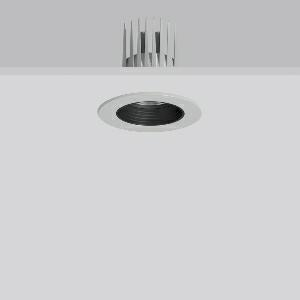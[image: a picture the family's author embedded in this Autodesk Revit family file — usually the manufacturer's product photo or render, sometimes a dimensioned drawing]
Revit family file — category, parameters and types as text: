
# Revit family: heledon_mini_e_901743_004_2_247d
name_source: partatom
category: Lighting Fixtures
units: mm (PartAtom-declared; Revit-internal decimal feet)

## family parameters
Cut with Voids When Loaded = No
Host = Face
Light Source = No
Part Type = Normal
Room Calculation Point = No
Round Connector Dimension = Use Diameter
Shared = No

## types (1)
- HELEDON mini E (1 x LED Modul 927, 2100 lm, 2700)
    Apparent Load = 20 VA
    Approval mark = CE
    CIE Flux Codes = 99 100 100 100 100
    Color Rendering = 92
    Color Temperature = 2700
    Default Elevation = 1800 mm
    Description = Series: HELEDON mini
Round recessed downlight. Housing: die-cast aluminium, powder-coated. Black plastic ring and recessed LED to prevent glare from the side. Optical assembly with lens made of plastic (polycarbonate) for the best homogeneous light distribution - can be changed without tools. Best colour rendering index Ra>90. Suitable for Recessed ceiling mounting. Installation without tools thanks to spring fastening system. Including separate LED converter with connecting cable 600 mm.High quality converter without flickering and stroboscopic effect. Through-wiring box (5 pole) available as accessory. The following accessories can be mounted without use of tools: interchangeable lenses, decorative glasses, honeycomb louvre, clear and frosted diffusers, white interchangeable plastic ring. 
Colour: silver
Diameter: 124 mm
Height: 3 mm
Cut-out diameter: 114 mm
Recess height: 170 mm
Luminaire: recess height: 120 mm
Lamp: LED
Socket: without socket
Colour temperature: 2700K
Colour rendering index (CRI): 92
System power: 20 W
Rated luminous flux: 2100 lm
Luminous efficiency: 105 lm/W
Control gear: Regulated power supply
Protection class: II
Type of protection: IP 20
    Height = 0 mm  [stored 0 ft]
    Lamp = 1 x LED Modul 927
    Lamp Light Flux = 2100 lm
    Lamp count = 1
    Length = 124 mm  [stored 0.406824 ft]
    Lifetime = 50000 h
    Luminous efficacy = 105 lm/W
    Manufacturer = RZB
    ModVariant = No
    Model = 901743.004.2
    Mounting Place = Ceiling
    Mounting Type = Recessed
    Number of Poles = 1
    OnlyDefault = Yes
    Power Factor = 1
    Product Name = HELEDON mini E
    Product group = Recessed downlights
    ProductGroupID = 402
    Protection Class = Protection class II
    Protection Degree = IP 20
    RLX_Detail_Level = 1
    RLX_Emergency_Light_Flux = 0 lm
    RLX_Emergency_Type = 0
    RLX_Emergency_Type_DB = No
    RlxData = <blob elided: 126573 chars, md5=3484c6cd>
    Socket = socket
    Standby Power = 0 W
    System Light Flux = 2100 lm
    System Power = 20 W
    Type Comments = Product without accessories
    Type Image = 901656.004.jpg
    URL = http://relux.com
    VarID = ---
    Voltage = 230 V
    Voltage Range = 220-240 V
    Weight = 0.00 kg
    Width = 0 mm  [stored 0 ft]

note: [stored X ft] marks values corroborated as IEEE doubles in the binary element streams (Revit-internal decimal feet)

## geometry (parser evidence)
native form markers: Blend x4, Sweep x11
no freeform markers — native parametric forms only
